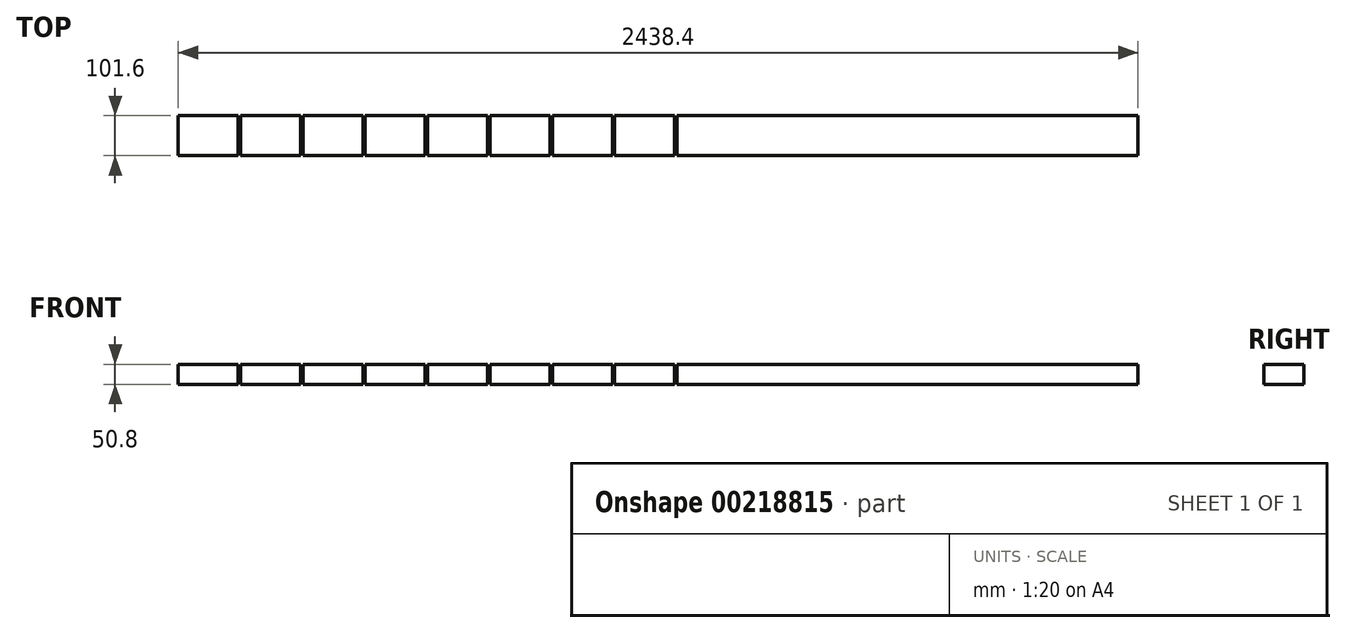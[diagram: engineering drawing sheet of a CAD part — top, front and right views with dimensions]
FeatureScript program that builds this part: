
annotation { "Feature Type Name" : "Feature", "Feature Type Description" : "" }
export const myFeature = defineFeature(function(context is Context, id is Id, definition is map)
    precondition{}
    {
        {
            var Q0;
            Q0=qCreatedBy(makeId("Top.planeOp"),FACE);
            var sketch = newSketch(context, id + "F0", { "sketchPlane" : qUnion([Q0])});
            skLineSegment(sketch, "E0.bottom", {"start": v(0, 0) * mm, "end": v(2438.4, 0) * mm});
            skLineSegment(sketch, "E0.top", {"start": v(0, -101.6) * mm, "end": v(2438.4, -101.6) * mm});
            skLineSegment(sketch, "E0.left", {"start": v(0, 0) * mm, "end": v(0, -101.6) * mm});
            skLineSegment(sketch, "E0.right", {"start": v(2438.4, 0) * mm, "end": v(2438.4, -101.6) * mm});
            skSolve(sketch);
        }
        {
            var Q0;
            Q0=makeQuery(id+"F0.imprint","IMPRINT",FACE,{"disambiguationData":[TD([[makeQuery(id+"F0.imprint","IMPRINT",EDGE,{"derivedFrom":sQuery(id+"F0.wireOp",EDGE,"E0.bottom")}),-1.0]])]});
            extrude(context, id + "F1", {"entities" : qUnion([Q0]), "depth" : 50.8 * mm});
        }
        {
            var Q0;
            Q0=makeQuery(id+"F1.opExtrude","CAP_FACE",FACE,{"disambiguationData":[OSD([sQuery(id+"F0.wireOp",EDGE,"E0.bottom"),sQuery(id+"F0.wireOp",EDGE,"E0.top"),sQuery(id+"F0.wireOp",EDGE,"E0.left"),sQuery(id+"F0.wireOp",EDGE,"E0.right")])],"isStart":false});
            var sketch = newSketch(context, id + "F2", { "sketchPlane" : qUnion([Q0])});
            skLineSegment(sketch, "E1.bottom", {"start": v(0, 0) * mm, "end": v(152.4, 0) * mm});
            skLineSegment(sketch, "E1.top", {"start": v(0, -101.6) * mm, "end": v(152.4, -101.6) * mm});
            skLineSegment(sketch, "E1.left", {"start": v(0, 0) * mm, "end": v(0, -101.6) * mm});
            skLineSegment(sketch, "E1.right", {"start": v(152.4, 0) * mm, "end": v(152.4, -101.6) * mm});
            skLineSegment(sketch, "E2.bottom", {"start": v(158.4, 0) * mm, "end": v(310.8, 0) * mm});
            skLineSegment(sketch, "E2.top", {"start": v(158.4, -101.6) * mm, "end": v(310.8, -101.6) * mm});
            skLineSegment(sketch, "E2.left", {"start": v(158.4, 0) * mm, "end": v(158.4, -101.6) * mm});
            skLineSegment(sketch, "E2.right", {"start": v(310.8, 0) * mm, "end": v(310.8, -101.6) * mm});
            skLineSegment(sketch, "E3.bottom", {"start": v(316.8, 0) * mm, "end": v(469.2, 0) * mm});
            skLineSegment(sketch, "E3.top", {"start": v(316.8, -101.6) * mm, "end": v(469.2, -101.6) * mm});
            skLineSegment(sketch, "E3.left", {"start": v(316.8, 0) * mm, "end": v(316.8, -101.6) * mm});
            skLineSegment(sketch, "E3.right", {"start": v(469.2, 0) * mm, "end": v(469.2, -101.6) * mm});
            skLineSegment(sketch, "E4.bottom", {"start": v(475.2, 0) * mm, "end": v(627.6, 0) * mm});
            skLineSegment(sketch, "E4.top", {"start": v(475.2, -101.6) * mm, "end": v(627.6, -101.6) * mm});
            skLineSegment(sketch, "E4.left", {"start": v(475.2, 0) * mm, "end": v(475.2, -101.6) * mm});
            skLineSegment(sketch, "E4.right", {"start": v(627.6, 0) * mm, "end": v(627.6, -101.6) * mm});
            skLineSegment(sketch, "E5.bottom", {"start": v(633.6, 0) * mm, "end": v(786, 0) * mm});
            skLineSegment(sketch, "E5.top", {"start": v(633.6, -101.6) * mm, "end": v(786, -101.6) * mm});
            skLineSegment(sketch, "E5.left", {"start": v(633.6, 0) * mm, "end": v(633.6, -101.6) * mm});
            skLineSegment(sketch, "E5.right", {"start": v(786, 0) * mm, "end": v(786, -101.6) * mm});
            skLineSegment(sketch, "E6.bottom", {"start": v(792, 0) * mm, "end": v(944.4, 0) * mm});
            skLineSegment(sketch, "E6.top", {"start": v(792, -101.6) * mm, "end": v(944.4, -101.6) * mm});
            skLineSegment(sketch, "E6.left", {"start": v(792, 0) * mm, "end": v(792, -101.6) * mm});
            skLineSegment(sketch, "E6.right", {"start": v(944.4, 0) * mm, "end": v(944.4, -101.6) * mm});
            skLineSegment(sketch, "E7.bottom", {"start": v(950.4, 0) * mm, "end": v(1102.8, 0) * mm});
            skLineSegment(sketch, "E7.top", {"start": v(950.4, -101.6) * mm, "end": v(1102.8, -101.6) * mm});
            skLineSegment(sketch, "E7.left", {"start": v(950.4, 0) * mm, "end": v(950.4, -101.6) * mm});
            skLineSegment(sketch, "E7.right", {"start": v(1102.8, 0) * mm, "end": v(1102.8, -101.6) * mm});
            skLineSegment(sketch, "E8.bottom", {"start": v(1108.8, 0) * mm, "end": v(1261.2, 0) * mm});
            skLineSegment(sketch, "E8.top", {"start": v(1108.8, -101.6) * mm, "end": v(1261.2, -101.6) * mm});
            skLineSegment(sketch, "E8.left", {"start": v(1108.8, 0) * mm, "end": v(1108.8, -101.6) * mm});
            skLineSegment(sketch, "E8.right", {"start": v(1261.2, 0) * mm, "end": v(1261.2, -101.6) * mm});
            skLineSegment(sketch, "E9.bottom", {"start": v(1267.2, 0) * mm, "end": v(1419.6, 0) * mm});
            skLineSegment(sketch, "E9.top", {"start": v(1267.2, -101.6) * mm, "end": v(1419.6, -101.6) * mm});
            skLineSegment(sketch, "E9.left", {"start": v(1267.2, 0) * mm, "end": v(1267.2, -101.6) * mm});
            skLineSegment(sketch, "E9.right", {"start": v(1419.6, 0) * mm, "end": v(1419.6, -101.6) * mm});
            skSolve(sketch);
        }
        {
            var Q0;
            {var subQ0=sQuery(id+"F2.wireOp",EDGE,"E1.right");Q0=makeQuery(id+"F2.imprint","IMPRINT",FACE,{"disambiguationData":[TD([[makeQuery(id+"F2.imprint","IMPRINT",EDGE,{"derivedFrom":subQ0}),1.0]])]});}
            var Q1;
            {var subQ0=sQuery(id+"F2.wireOp",EDGE,"E2.right");Q1=makeQuery(id+"F2.imprint","IMPRINT",FACE,{"disambiguationData":[TD([[makeQuery(id+"F2.imprint","IMPRINT",EDGE,{"derivedFrom":subQ0}),1.0]])]});}
            var Q2;
            {var subQ0=sQuery(id+"F2.wireOp",EDGE,"E3.right");Q2=makeQuery(id+"F2.imprint","IMPRINT",FACE,{"disambiguationData":[TD([[makeQuery(id+"F2.imprint","IMPRINT",EDGE,{"derivedFrom":subQ0}),1.0]])]});}
            var Q3;
            {var subQ0=sQuery(id+"F2.wireOp",EDGE,"E4.right");Q3=makeQuery(id+"F2.imprint","IMPRINT",FACE,{"disambiguationData":[TD([[makeQuery(id+"F2.imprint","IMPRINT",EDGE,{"derivedFrom":subQ0}),1.0]])]});}
            var Q4;
            {var subQ0=sQuery(id+"F2.wireOp",EDGE,"E5.right");Q4=makeQuery(id+"F2.imprint","IMPRINT",FACE,{"disambiguationData":[TD([[makeQuery(id+"F2.imprint","IMPRINT",EDGE,{"derivedFrom":subQ0}),1.0]])]});}
            var Q5;
            {var subQ0=sQuery(id+"F2.wireOp",EDGE,"E6.right");Q5=makeQuery(id+"F2.imprint","IMPRINT",FACE,{"disambiguationData":[TD([[makeQuery(id+"F2.imprint","IMPRINT",EDGE,{"derivedFrom":subQ0}),1.0]])]});}
            var Q6;
            {var subQ0=sQuery(id+"F2.wireOp",EDGE,"E7.right");Q6=makeQuery(id+"F2.imprint","IMPRINT",FACE,{"disambiguationData":[TD([[makeQuery(id+"F2.imprint","IMPRINT",EDGE,{"derivedFrom":subQ0}),1.0]])]});}
            var Q7;
            {var subQ0=sQuery(id+"F2.wireOp",EDGE,"E8.right");Q7=makeQuery(id+"F2.imprint","IMPRINT",FACE,{"disambiguationData":[TD([[makeQuery(id+"F2.imprint","IMPRINT",EDGE,{"derivedFrom":subQ0}),1.0]])]});}
            extrude(context, id + "F3", {"entities" : qUnion([Q0, Q1, Q2, Q3, Q4, Q5, Q6, Q7]), "operationType" : NewBodyOperationType.REMOVE, "oppositeDirection" : true, "depth" : 50.8 * mm});
        }
    });
